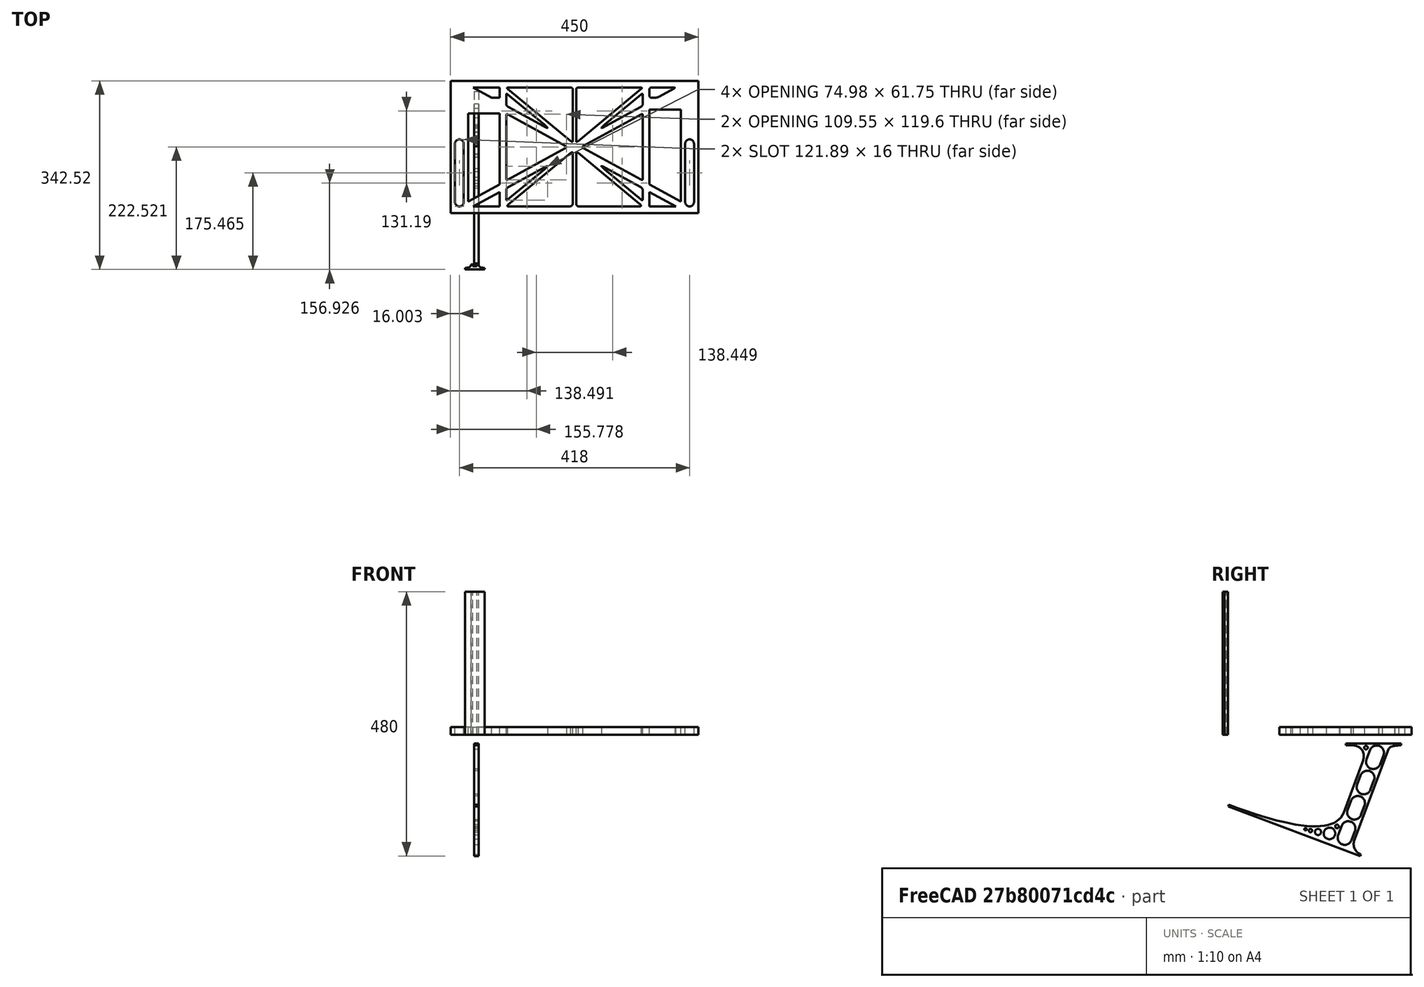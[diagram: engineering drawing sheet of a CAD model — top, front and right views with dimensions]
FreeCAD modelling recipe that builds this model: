
FCSTD DOCUMENT  (FreeCAD 0.19R0.19.2)
Label: laptopStand099
License: All rights reserved
LicenseURL: http://en.wikipedia.org/wiki/All_rights_reserved
objects: Sketcher::SketchObject×3, Part::Extrusion×3
note: 6 computed .brp shape members not serialized (recipe doc carries the construction recipe); baked Part::Feature solids carry a one-line shape summary decoded from their .brp

FEATURE [Sketcher::SketchObject] Sketch
  FullyConstrained = true
  sketch-geometry (268):
    g0: LineSegment StartX=-10.9272 StartY=-82.7794 StartZ=0 EndX=46.0728 EndY=-51.4823 EndZ=0
    g1: LineSegment StartX=366.073 StartY=-91.7794 StartZ=0 EndX=318.073 EndY=-65.424 EndZ=0
    g2: LineSegment StartX=-10.9272 StartY=77.3346 StartZ=0 EndX=-10.9272 EndY=-82.7794 EndZ=0
    g3: LineSegment StartX=375.073 StartY=-82.7794 StartZ=0 EndX=375.073 EndY=83.9235 EndZ=0
    g4: LineSegment StartX=-1.92719 StartY=-91.7794 StartZ=0 EndX=46.0728 EndY=-91.7794 EndZ=0
    g5: LineSegment StartX=318.073 StartY=83.9235 StartZ=0 EndX=318.073 EndY=-51.4823 EndZ=0
    g6: LineSegment StartX=318.073 StartY=-51.4823 StartZ=0 EndX=375.073 EndY=-82.7794 EndZ=0
    g7: LineSegment StartX=318.073 StartY=-65.424 StartZ=0 EndX=318.073 EndY=-91.7794 EndZ=0
    g8: LineSegment StartX=318.073 StartY=-91.7794 StartZ=0 EndX=366.073 EndY=-91.7794 EndZ=0
    g9: LineSegment StartX=46.0728 StartY=-65.424 StartZ=0 EndX=-1.92719 EndY=-91.7794 EndZ=0
    g10: LineSegment StartX=46.0728 StartY=-65.424 StartZ=0 EndX=46.0728 EndY=-91.7794 EndZ=0
    g11: LineSegment StartX=46.0728 StartY=77.3346 StartZ=0 EndX=46.0728 EndY=-51.4823 EndZ=0
    g12: LineSegment StartX=-42.9272 StartY=136.221 StartZ=0 EndX=-42.9272 EndY=-103.779 EndZ=0
    g13: LineSegment StartX=407.073 StartY=136.221 StartZ=0 EndX=407.073 EndY=-103.779 EndZ=0
    g14: ArcOfCircle CenterX=-26.9272 CenterY=22.1087 CenterZ=0 NormalX=0 NormalY=0 NormalZ=1 AngleXU=0 Radius=8 StartAngle=1e-16 EndAngle=3.14159
    g15: ArcOfCircle CenterX=-26.9272 CenterY=-83.7794 CenterZ=0 NormalX=0 NormalY=0 NormalZ=1 AngleXU=0 Radius=8 StartAngle=3.14159 EndAngle=6.28319
    g16: LineSegment StartX=-34.9272 StartY=22.1087 StartZ=0 EndX=-34.9272 EndY=-83.7794 EndZ=0
    g17: LineSegment StartX=-18.9272 StartY=22.1087 StartZ=0 EndX=-18.9272 EndY=-83.7794 EndZ=0
    g18: ArcOfCircle CenterX=391.073 CenterY=22.1087 CenterZ=0 NormalX=0 NormalY=0 NormalZ=1 AngleXU=0 Radius=8 StartAngle=-4.4e-15 EndAngle=3.14159
    g19: LineSegment StartX=399.073 StartY=22.1087 StartZ=0 EndX=399.073 EndY=-83.7794 EndZ=0
    g20: LineSegment StartX=383.073 StartY=22.1087 StartZ=0 EndX=383.073 EndY=-83.7794 EndZ=0
    g21: ArcOfCircle CenterX=391.073 CenterY=-83.7794 CenterZ=0 NormalX=0 NormalY=0 NormalZ=1 AngleXU=0 Radius=8 StartAngle=3.14159 EndAngle=6.28319
    g22: Circle CenterX=175.022 CenterY=27.0628 CenterZ=0 NormalX=0 NormalY=0 NormalZ=1 AngleXU=0 Radius=1
    g23: Circle CenterX=179.022 CenterY=24.8665 CenterZ=0 NormalX=0 NormalY=0 NormalZ=1 AngleXU=0 Radius=1
    g24: Circle CenterX=179.022 CenterY=27.0628 CenterZ=0 NormalX=0 NormalY=0 NormalZ=1 AngleXU=0 Radius=1
    g25: BSplineCurve PolesCount=3 KnotsCount=2 Degree=2 IsPeriodic=0
    g26: GeomPoint X=175.022 Y=27.0628 Z=0
    g27: GeomPoint X=179.022 Y=27.0628 Z=0
    g28: Circle CenterX=189.124 CenterY=27.0628 CenterZ=0 NormalX=0 NormalY=0 NormalZ=1 AngleXU=0 Radius=1
    g29: Circle CenterX=185.124 CenterY=24.8665 CenterZ=0 NormalX=0 NormalY=0 NormalZ=1 AngleXU=0 Radius=1
    g30: Circle CenterX=185.124 CenterY=27.0628 CenterZ=0 NormalX=0 NormalY=0 NormalZ=1 AngleXU=0 Radius=1
    g31: BSplineCurve PolesCount=3 KnotsCount=2 Degree=2 IsPeriodic=0
    g32: GeomPoint X=189.124 Y=27.0628 Z=0
    g33: GeomPoint X=185.124 Y=27.0628 Z=0
    g34: Circle CenterX=175.022 CenterY=5.37834 CenterZ=0 NormalX=0 NormalY=0 NormalZ=1 AngleXU=0 Radius=1
    g35: Circle CenterX=179.022 CenterY=7.57463 CenterZ=0 NormalX=0 NormalY=0 NormalZ=1 AngleXU=0 Radius=1
    g36: Circle CenterX=179.022 CenterY=5.34704 CenterZ=0 NormalX=0 NormalY=0 NormalZ=1 AngleXU=0 Radius=1
    g37: BSplineCurve PolesCount=3 KnotsCount=2 Degree=2 IsPeriodic=0
    g38: GeomPoint X=175.022 Y=5.37834 Z=0
    g39: GeomPoint X=179.022 Y=5.34704 Z=0
    g40: Circle CenterX=189.124 CenterY=5.37834 CenterZ=0 NormalX=0 NormalY=0 NormalZ=1 AngleXU=0 Radius=1
    g41: Circle CenterX=185.124 CenterY=7.57463 CenterZ=0 NormalX=0 NormalY=0 NormalZ=1 AngleXU=0 Radius=1
    g42: Circle CenterX=185.124 CenterY=5.34704 CenterZ=0 NormalX=0 NormalY=0 NormalZ=1 AngleXU=0 Radius=1
    g43: BSplineCurve PolesCount=3 KnotsCount=2 Degree=2 IsPeriodic=0
    g44: GeomPoint X=189.124 Y=5.37834 Z=0
    g45: GeomPoint X=185.124 Y=5.34704 Z=0
    g46: Circle CenterX=165.871 CenterY=18.1458 CenterZ=0 NormalX=0 NormalY=0 NormalZ=1 AngleXU=0 Radius=1
    g47: Circle CenterX=169.377 CenterY=16.2206 CenterZ=0 NormalX=0 NormalY=0 NormalZ=1 AngleXU=0 Radius=1
    g48: Circle CenterX=165.871 CenterY=14.2954 CenterZ=0 NormalX=0 NormalY=0 NormalZ=1 AngleXU=0 Radius=1
    g49: BSplineCurve PolesCount=3 KnotsCount=2 Degree=2 IsPeriodic=0
    g50: GeomPoint X=165.871 Y=18.1458 Z=0
    g51: GeomPoint X=165.871 Y=14.2954 Z=0
    g52: Circle CenterX=198.275 CenterY=18.1458 CenterZ=0 NormalX=0 NormalY=0 NormalZ=1 AngleXU=0 Radius=1
    g53: Circle CenterX=194.768 CenterY=16.2206 CenterZ=0 NormalX=0 NormalY=0 NormalZ=1 AngleXU=0 Radius=1
    g54: Circle CenterX=198.275 CenterY=14.2954 CenterZ=0 NormalX=0 NormalY=0 NormalZ=1 AngleXU=0 Radius=1
    g55: BSplineCurve PolesCount=3 KnotsCount=2 Degree=2 IsPeriodic=0
    g56: GeomPoint X=198.275 Y=18.1458 Z=0
    g57: GeomPoint X=198.275 Y=14.2954 Z=0
    g58: LineSegment StartX=407.073 StartY=-103.779 StartZ=0 EndX=-42.9272 EndY=-103.779 EndZ=0
    g59: LineSegment StartX=407.073 StartY=136.221 StartZ=0 EndX=-42.9272 EndY=136.221 EndZ=0
    g60: LineSegment StartX=46.0728 StartY=77.3346 StartZ=0 EndX=-10.9272 EndY=77.3346 EndZ=0
    g61: LineSegment StartX=46.0728 StartY=105.865 StartZ=0 EndX=31.5028 EndY=105.865 EndZ=0
    g62: LineSegment StartX=46.0728 StartY=124.221 StartZ=0 EndX=46.0728 EndY=105.865 EndZ=0
    g63: LineSegment StartX=-1.92719 StartY=124.221 StartZ=0 EndX=31.5028 EndY=105.865 EndZ=0
    g64: LineSegment StartX=46.0728 StartY=124.221 StartZ=0 EndX=-1.92719 EndY=124.221 EndZ=0
    g65: LineSegment StartX=318.073 StartY=83.9235 StartZ=0 EndX=375.073 EndY=83.9235 EndZ=0
    g66: Circle CenterX=125.607 CenterY=54.1951 CenterZ=0 NormalX=0 NormalY=0 NormalZ=1 AngleXU=0 Radius=1
    g67: Circle CenterX=139.632 CenterY=46.4944 CenterZ=0 NormalX=0 NormalY=0 NormalZ=1 AngleXU=0 Radius=1
    g68: Circle CenterX=127.326 CenterY=56.7187 CenterZ=0 NormalX=0 NormalY=0 NormalZ=1 AngleXU=0 Radius=1
    g69: BSplineCurve PolesCount=3 KnotsCount=2 Degree=2 IsPeriodic=0
    g70: GeomPoint X=125.607 Y=54.1951 Z=0
    g71: GeomPoint X=127.326 Y=56.7187 Z=0
    g72: Circle CenterX=236.821 CenterY=56.7187 CenterZ=0 NormalX=0 NormalY=0 NormalZ=1 AngleXU=0 Radius=1
    g73: Circle CenterX=224.513 CenterY=46.4944 CenterZ=0 NormalX=0 NormalY=0 NormalZ=1 AngleXU=0 Radius=1
    g74: Circle CenterX=238.538 CenterY=54.1951 CenterZ=0 NormalX=0 NormalY=0 NormalZ=1 AngleXU=0 Radius=1
    g75: BSplineCurve PolesCount=3 KnotsCount=2 Degree=2 IsPeriodic=0
    g76: GeomPoint X=236.821 Y=56.7187 Z=0
    g77: GeomPoint X=238.538 Y=54.1951 Z=0
    g78: Circle CenterX=238.538 CenterY=-21.7539 CenterZ=0 NormalX=0 NormalY=0 NormalZ=1 AngleXU=0 Radius=1
    g79: Circle CenterX=224.513 CenterY=-14.0532 CenterZ=0 NormalX=0 NormalY=0 NormalZ=1 AngleXU=0 Radius=1
    g80: Circle CenterX=236.821 CenterY=-24.2775 CenterZ=0 NormalX=0 NormalY=0 NormalZ=1 AngleXU=0 Radius=1
    g81: BSplineCurve PolesCount=3 KnotsCount=2 Degree=2 IsPeriodic=0
    g82: GeomPoint X=238.538 Y=-21.7539 Z=0
    g83: GeomPoint X=236.821 Y=-24.2775 Z=0
    g84: Circle CenterX=125.607 CenterY=-21.7539 CenterZ=0 NormalX=0 NormalY=0 NormalZ=1 AngleXU=0 Radius=1
    g85: Circle CenterX=139.632 CenterY=-14.0532 CenterZ=0 NormalX=0 NormalY=0 NormalZ=1 AngleXU=0 Radius=1
    g86: Circle CenterX=127.325 CenterY=-24.2775 CenterZ=0 NormalX=0 NormalY=0 NormalZ=1 AngleXU=0 Radius=1
    g87: BSplineCurve PolesCount=3 KnotsCount=2 Degree=2 IsPeriodic=0
    g88: GeomPoint X=125.607 Y=-21.7539 Z=0
    g89: GeomPoint X=127.325 Y=-24.2775 Z=0
    g90: Circle CenterX=302.996 CenterY=111.695 CenterZ=0 NormalX=0 NormalY=0 NormalZ=1 AngleXU=0 Radius=1
    g91: Circle CenterX=306.073 CenterY=114.251 CenterZ=0 NormalX=0 NormalY=0 NormalZ=1 AngleXU=0 Radius=1
    g92: Circle CenterX=306.073 CenterY=110.251 CenterZ=0 NormalX=0 NormalY=0 NormalZ=1 AngleXU=0 Radius=1
    g93: BSplineCurve PolesCount=3 KnotsCount=2 Degree=2 IsPeriodic=0
    g94: GeomPoint X=302.996 Y=111.695 Z=0
    g95: GeomPoint X=306.073 Y=110.251 Z=0
    g96: Circle CenterX=306.073 CenterY=95.2763 CenterZ=0 NormalX=0 NormalY=0 NormalZ=1 AngleXU=0 Radius=1
    g97: Circle CenterX=306.073 CenterY=91.2763 CenterZ=0 NormalX=0 NormalY=0 NormalZ=1 AngleXU=0 Radius=1
    g98: Circle CenterX=302.567 CenterY=89.3511 CenterZ=0 NormalX=0 NormalY=0 NormalZ=1 AngleXU=0 Radius=1
    g99: BSplineCurve PolesCount=3 KnotsCount=2 Degree=2 IsPeriodic=0
    g100: GeomPoint X=306.073 Y=95.2763 Z=0
    g101: GeomPoint X=302.567 Y=89.3511 Z=0
    g102: LineSegment StartX=306.073 StartY=110.251 StartZ=0 EndX=306.073 EndY=95.2763 EndZ=0
    g103: LineSegment StartX=302.996 StartY=111.695 StartZ=0 EndX=236.821 EndY=56.7187 EndZ=0
    g104: LineSegment StartX=238.538 StartY=54.1951 StartZ=0 EndX=302.567 EndY=89.3511 EndZ=0
    g105: Circle CenterX=61.1496 CenterY=111.695 CenterZ=0 NormalX=0 NormalY=0 NormalZ=1 AngleXU=0 Radius=1
    g106: Circle CenterX=58.0728 CenterY=114.251 CenterZ=0 NormalX=0 NormalY=0 NormalZ=1 AngleXU=0 Radius=1
    g107: Circle CenterX=58.0728 CenterY=110.251 CenterZ=0 NormalX=0 NormalY=0 NormalZ=1 AngleXU=0 Radius=1
    g108: BSplineCurve PolesCount=3 KnotsCount=2 Degree=2 IsPeriodic=0
    g109: GeomPoint X=61.1496 Y=111.695 Z=0
    g110: GeomPoint X=58.0728 Y=110.251 Z=0
    g111: Circle CenterX=61.5791 CenterY=89.3511 CenterZ=0 NormalX=0 NormalY=0 NormalZ=1 AngleXU=0 Radius=1
    g112: Circle CenterX=58.0728 CenterY=91.2763 CenterZ=0 NormalX=0 NormalY=0 NormalZ=1 AngleXU=0 Radius=1
    g113: Circle CenterX=58.0728 CenterY=95.2763 CenterZ=0 NormalX=0 NormalY=0 NormalZ=1 AngleXU=0 Radius=1
    g114: BSplineCurve PolesCount=3 KnotsCount=2 Degree=2 IsPeriodic=0
    g115: GeomPoint X=61.5791 Y=89.3511 Z=0
    g116: GeomPoint X=58.0728 Y=95.2763 Z=0
    g117: LineSegment StartX=58.0728 StartY=110.251 StartZ=0 EndX=58.0728 EndY=95.2763 EndZ=0
    g118: LineSegment StartX=61.1496 StartY=111.695 StartZ=0 EndX=127.326 EndY=56.7187 EndZ=0
    g119: LineSegment StartX=125.607 StartY=54.1951 StartZ=0 EndX=61.5791 EndY=89.3511 EndZ=0
    g120: Circle CenterX=61.5791 CenterY=-56.9099 CenterZ=0 NormalX=0 NormalY=0 NormalZ=1 AngleXU=0 Radius=1
    g121: Circle CenterX=58.0728 CenterY=-58.8351 CenterZ=0 NormalX=0 NormalY=0 NormalZ=1 AngleXU=0 Radius=1
    g122: Circle CenterX=58.0728 CenterY=-62.8351 CenterZ=0 NormalX=0 NormalY=0 NormalZ=1 AngleXU=0 Radius=1
    g123: BSplineCurve PolesCount=3 KnotsCount=2 Degree=2 IsPeriodic=0
    g124: GeomPoint X=61.5791 Y=-56.9099 Z=0
    g125: GeomPoint X=58.0728 Y=-62.8351 Z=0
    g126: Circle CenterX=58.0728 CenterY=-77.8102 CenterZ=0 NormalX=0 NormalY=0 NormalZ=1 AngleXU=0 Radius=1
    g127: Circle CenterX=58.0728 CenterY=-81.8102 CenterZ=0 NormalX=0 NormalY=0 NormalZ=1 AngleXU=0 Radius=1
    g128: Circle CenterX=61.1496 CenterY=-79.2541 CenterZ=0 NormalX=0 NormalY=0 NormalZ=1 AngleXU=0 Radius=1
    g129: BSplineCurve PolesCount=3 KnotsCount=2 Degree=2 IsPeriodic=0
    g130: GeomPoint X=58.0728 Y=-77.8102 Z=0
    g131: GeomPoint X=61.1496 Y=-79.2541 Z=0
    g132: LineSegment StartX=58.0728 StartY=-62.8351 StartZ=0 EndX=58.0728 EndY=-77.8102 EndZ=0
    g133: LineSegment StartX=61.1496 StartY=-79.2541 StartZ=0 EndX=127.325 EndY=-24.2775 EndZ=0
    g134: LineSegment StartX=125.607 StartY=-21.7539 StartZ=0 EndX=61.5791 EndY=-56.9099 EndZ=0
    g135: Circle CenterX=302.567 CenterY=-56.9099 CenterZ=0 NormalX=0 NormalY=0 NormalZ=1 AngleXU=0 Radius=1
    g136: Circle CenterX=306.073 CenterY=-58.8351 CenterZ=0 NormalX=0 NormalY=0 NormalZ=1 AngleXU=0 Radius=1
    g137: Circle CenterX=306.073 CenterY=-62.8351 CenterZ=0 NormalX=0 NormalY=0 NormalZ=1 AngleXU=0 Radius=1
    g138: BSplineCurve PolesCount=3 KnotsCount=2 Degree=2 IsPeriodic=0
    g139: GeomPoint X=302.567 Y=-56.9099 Z=0
    g140: GeomPoint X=306.073 Y=-62.8351 Z=0
    g141: Circle CenterX=302.996 CenterY=-79.2541 CenterZ=0 NormalX=0 NormalY=0 NormalZ=1 AngleXU=0 Radius=1
    g142: Circle CenterX=306.073 CenterY=-81.8102 CenterZ=0 NormalX=0 NormalY=0 NormalZ=1 AngleXU=0 Radius=1
    g143: Circle CenterX=306.073 CenterY=-77.8102 CenterZ=0 NormalX=0 NormalY=0 NormalZ=1 AngleXU=0 Radius=1
    g144: BSplineCurve PolesCount=3 KnotsCount=2 Degree=2 IsPeriodic=0
    g145: GeomPoint X=302.996 Y=-79.2541 Z=0
    g146: GeomPoint X=306.073 Y=-77.8102 Z=0
    g147: LineSegment StartX=306.073 StartY=-62.8351 StartZ=0 EndX=306.073 EndY=-77.8102 EndZ=0
    g148: LineSegment StartX=302.996 StartY=-79.2541 StartZ=0 EndX=236.821 EndY=-24.2775 EndZ=0
    g149: LineSegment StartX=238.538 StartY=-21.7539 StartZ=0 EndX=302.567 EndY=-56.9099 EndZ=0
    g150: Circle CenterX=61.6457 CenterY=-88.8112 CenterZ=0 NormalX=0 NormalY=0 NormalZ=1 AngleXU=0 Radius=1
    g151: Circle CenterX=58.0728 CenterY=-91.7794 CenterZ=0 NormalX=0 NormalY=0 NormalZ=1 AngleXU=0 Radius=1
    g152: Circle CenterX=63.9135 CenterY=-91.7794 CenterZ=0 NormalX=0 NormalY=0 NormalZ=1 AngleXU=0 Radius=1
    g153: BSplineCurve PolesCount=3 KnotsCount=2 Degree=2 IsPeriodic=0
    g154: GeomPoint X=61.6457 Y=-88.8112 Z=0
    g155: GeomPoint X=63.9135 Y=-91.7794 Z=0
    g156: Circle CenterX=179.022 CenterY=-85.8163 CenterZ=0 NormalX=0 NormalY=0 NormalZ=1 AngleXU=0 Radius=1
    g157: Circle CenterX=179.022 CenterY=-91.7794 CenterZ=0 NormalX=0 NormalY=0 NormalZ=1 AngleXU=0 Radius=1
    g158: Circle CenterX=171.895 CenterY=-91.7794 CenterZ=0 NormalX=0 NormalY=0 NormalZ=1 AngleXU=0 Radius=1
    g159: BSplineCurve PolesCount=3 KnotsCount=2 Degree=2 IsPeriodic=0
    g160: GeomPoint X=179.022 Y=-85.8163 Z=0
    g161: GeomPoint X=171.895 Y=-91.7794 Z=0
    g162: Circle CenterX=185.124 CenterY=-86.2028 CenterZ=0 NormalX=0 NormalY=0 NormalZ=1 AngleXU=0 Radius=1
    g163: Circle CenterX=185.124 CenterY=-91.7794 CenterZ=0 NormalX=0 NormalY=0 NormalZ=1 AngleXU=0 Radius=1
    g164: Circle CenterX=191.747 CenterY=-91.7794 CenterZ=0 NormalX=0 NormalY=0 NormalZ=1 AngleXU=0 Radius=1
    g165: BSplineCurve PolesCount=3 KnotsCount=2 Degree=2 IsPeriodic=0
    g166: GeomPoint X=185.124 Y=-86.2028 Z=0
    g167: GeomPoint X=191.747 Y=-91.7794 Z=0
    g168: Circle CenterX=299.888 CenterY=-86.6413 CenterZ=0 NormalX=0 NormalY=0 NormalZ=1 AngleXU=0 Radius=1
    g169: Circle CenterX=306.073 CenterY=-91.7794 CenterZ=0 NormalX=0 NormalY=0 NormalZ=1 AngleXU=0 Radius=1
    g170: Circle CenterX=298.776 CenterY=-91.7794 CenterZ=0 NormalX=0 NormalY=0 NormalZ=1 AngleXU=0 Radius=1
    g171: BSplineCurve PolesCount=3 KnotsCount=2 Degree=2 IsPeriodic=0
    g172: GeomPoint X=299.888 Y=-86.6413 Z=0
    g173: GeomPoint X=298.776 Y=-91.7794 Z=0
    g174: LineSegment StartX=189.124 StartY=5.37834 StartZ=0 EndX=299.888 EndY=-86.6413 EndZ=0
    g175: LineSegment StartX=298.776 StartY=-91.7794 StartZ=0 EndX=191.747 EndY=-91.7794 EndZ=0
    g176: LineSegment StartX=185.124 StartY=-86.2028 StartZ=0 EndX=185.124 EndY=5.34704 EndZ=0
    g177: LineSegment StartX=179.022 StartY=5.34704 StartZ=0 EndX=179.022 EndY=-85.8163 EndZ=0
    g178: LineSegment StartX=171.895 StartY=-91.7794 StartZ=0 EndX=63.9135 EndY=-91.7794 EndZ=0
    g179: LineSegment StartX=61.6457 StartY=-88.8112 StartZ=0 EndX=175.022 EndY=5.37834 EndZ=0
    g180: Circle CenterX=302.073 CenterY=124.221 CenterZ=0 NormalX=0 NormalY=0 NormalZ=1 AngleXU=0 Radius=1
    g181: Circle CenterX=306.073 CenterY=124.221 CenterZ=0 NormalX=0 NormalY=0 NormalZ=1 AngleXU=0 Radius=1
    g182: Circle CenterX=302.996 CenterY=121.665 CenterZ=0 NormalX=0 NormalY=0 NormalZ=1 AngleXU=0 Radius=1
    g183: BSplineCurve PolesCount=3 KnotsCount=2 Degree=2 IsPeriodic=0
    g184: GeomPoint X=302.073 Y=124.221 Z=0
    g185: GeomPoint X=302.996 Y=121.665 Z=0
    g186: Circle CenterX=189.124 CenterY=124.221 CenterZ=0 NormalX=0 NormalY=0 NormalZ=1 AngleXU=0 Radius=1
    g187: Circle CenterX=185.124 CenterY=124.221 CenterZ=0 NormalX=0 NormalY=0 NormalZ=1 AngleXU=0 Radius=1
    g188: Circle CenterX=185.124 CenterY=120.221 CenterZ=0 NormalX=0 NormalY=0 NormalZ=1 AngleXU=0 Radius=1
    g189: BSplineCurve PolesCount=3 KnotsCount=2 Degree=2 IsPeriodic=0
    g190: GeomPoint X=189.124 Y=124.221 Z=0
    g191: GeomPoint X=185.124 Y=120.221 Z=0
    g192: Circle CenterX=175.022 CenterY=124.221 CenterZ=0 NormalX=0 NormalY=0 NormalZ=1 AngleXU=0 Radius=1
    g193: Circle CenterX=179.022 CenterY=124.221 CenterZ=0 NormalX=0 NormalY=0 NormalZ=1 AngleXU=0 Radius=1
    g194: Circle CenterX=179.022 CenterY=120.221 CenterZ=0 NormalX=0 NormalY=0 NormalZ=1 AngleXU=0 Radius=1
    g195: BSplineCurve PolesCount=3 KnotsCount=2 Degree=2 IsPeriodic=0
    g196: GeomPoint X=175.022 Y=124.221 Z=0
    g197: GeomPoint X=179.022 Y=120.221 Z=0
    g198: Circle CenterX=62.0728 CenterY=124.221 CenterZ=0 NormalX=0 NormalY=0 NormalZ=1 AngleXU=0 Radius=1
    g199: Circle CenterX=58.0728 CenterY=124.221 CenterZ=0 NormalX=0 NormalY=0 NormalZ=1 AngleXU=0 Radius=1
    g200: Circle CenterX=61.1496 CenterY=121.665 CenterZ=0 NormalX=0 NormalY=0 NormalZ=1 AngleXU=0 Radius=1
    g201: BSplineCurve PolesCount=3 KnotsCount=2 Degree=2 IsPeriodic=0
    g202: GeomPoint X=62.0728 Y=124.221 Z=0
    g203: GeomPoint X=61.1496 Y=121.665 Z=0
    g204: LineSegment StartX=62.0728 StartY=124.221 StartZ=0 EndX=175.022 EndY=124.221 EndZ=0
    g205: LineSegment StartX=179.022 StartY=120.221 StartZ=0 EndX=179.022 EndY=27.0628 EndZ=0
    g206: LineSegment StartX=185.124 StartY=27.0628 StartZ=0 EndX=185.124 EndY=120.221 EndZ=0
    g207: LineSegment StartX=189.124 StartY=124.221 StartZ=0 EndX=302.073 EndY=124.221 EndZ=0
    g208: LineSegment StartX=302.996 StartY=121.665 StartZ=0 EndX=189.124 EndY=27.0628 EndZ=0
    g209: LineSegment StartX=175.022 StartY=27.0628 StartZ=0 EndX=61.1496 EndY=121.665 EndZ=0
    g210: Circle CenterX=61.5791 CenterY=75.4095 CenterZ=0 NormalX=0 NormalY=0 NormalZ=1 AngleXU=0 Radius=1
    g211: Circle CenterX=58.0728 CenterY=77.3346 CenterZ=0 NormalX=0 NormalY=0 NormalZ=1 AngleXU=0 Radius=1
    g212: Circle CenterX=58.0728 CenterY=73.3346 CenterZ=0 NormalX=0 NormalY=0 NormalZ=1 AngleXU=0 Radius=1
    g213: BSplineCurve PolesCount=3 KnotsCount=2 Degree=2 IsPeriodic=0
    g214: GeomPoint X=61.5791 Y=75.4095 Z=0
    g215: GeomPoint X=58.0728 Y=73.3346 Z=0
    g216: Circle CenterX=58.0728 CenterY=-40.8935 CenterZ=0 NormalX=0 NormalY=0 NormalZ=1 AngleXU=0 Radius=1
    g217: Circle CenterX=58.0728 CenterY=-44.8935 CenterZ=0 NormalX=0 NormalY=0 NormalZ=1 AngleXU=0 Radius=1
    g218: Circle CenterX=61.5791 CenterY=-42.9683 CenterZ=0 NormalX=0 NormalY=0 NormalZ=1 AngleXU=0 Radius=1
    g219: BSplineCurve PolesCount=3 KnotsCount=2 Degree=2 IsPeriodic=0
    g220: GeomPoint X=58.0728 Y=-40.8935 Z=0
    g221: GeomPoint X=61.5791 Y=-42.9683 Z=0
    g222: LineSegment StartX=61.5791 StartY=-42.9683 StartZ=0 EndX=165.871 EndY=14.2954 EndZ=0
    g223: LineSegment StartX=165.871 StartY=18.1458 StartZ=0 EndX=61.5791 EndY=75.4095 EndZ=0
    g224: LineSegment StartX=58.0728 StartY=73.3346 StartZ=0 EndX=58.0728 EndY=-40.8935 EndZ=0
    g225: Circle CenterX=302.567 CenterY=-42.9683 CenterZ=0 NormalX=0 NormalY=0 NormalZ=1 AngleXU=0 Radius=1
    g226: Circle CenterX=306.073 CenterY=-44.8935 CenterZ=0 NormalX=0 NormalY=0 NormalZ=1 AngleXU=0 Radius=1
    g227: Circle CenterX=306.073 CenterY=-40.8935 CenterZ=0 NormalX=0 NormalY=0 NormalZ=1 AngleXU=0 Radius=1
    g228: BSplineCurve PolesCount=3 KnotsCount=2 Degree=2 IsPeriodic=0
    g229: GeomPoint X=302.567 Y=-42.9683 Z=0
    g230: GeomPoint X=306.073 Y=-40.8935 Z=0
    g231: Circle CenterX=306.073 CenterY=73.3346 CenterZ=0 NormalX=0 NormalY=0 NormalZ=1 AngleXU=0 Radius=1
    g232: Circle CenterX=306.073 CenterY=77.3346 CenterZ=0 NormalX=0 NormalY=0 NormalZ=1 AngleXU=0 Radius=1
    g233: Circle CenterX=302.567 CenterY=75.4095 CenterZ=0 NormalX=0 NormalY=0 NormalZ=1 AngleXU=0 Radius=1
    g234: BSplineCurve PolesCount=3 KnotsCount=2 Degree=2 IsPeriodic=0
    g235: GeomPoint X=306.073 Y=73.3346 Z=0
    g236: GeomPoint X=302.567 Y=75.4095 Z=0
    g237: LineSegment StartX=302.567 StartY=-42.9683 StartZ=0 EndX=198.275 EndY=14.2954 EndZ=0
    g238: LineSegment StartX=198.275 StartY=18.1458 StartZ=0 EndX=302.567 EndY=75.4095 EndZ=0
    g239: LineSegment StartX=306.073 StartY=73.3346 StartZ=0 EndX=306.073 EndY=-40.8935 EndZ=0
    g240: LineSegment StartX=322.073 StartY=105.865 StartZ=0 EndX=328.643 EndY=105.865 EndZ=0
    g241: LineSegment StartX=318.073 StartY=120.221 StartZ=0 EndX=318.073 EndY=109.865 EndZ=0
    g242: LineSegment StartX=336.157 StartY=107.779 StartZ=0 EndX=362.567 EndY=122.294 EndZ=0
    g243: Circle CenterX=362.073 CenterY=124.221 CenterZ=0 NormalX=0 NormalY=0 NormalZ=1 AngleXU=0 Radius=1
    g244: Circle CenterX=366.073 CenterY=124.221 CenterZ=0 NormalX=0 NormalY=0 NormalZ=1 AngleXU=0 Radius=1
    g245: Circle CenterX=362.567 CenterY=122.294 CenterZ=0 NormalX=0 NormalY=0 NormalZ=1 AngleXU=0 Radius=1
    g246: BSplineCurve PolesCount=3 KnotsCount=2 Degree=2 IsPeriodic=0
    g247: GeomPoint X=362.073 Y=124.221 Z=0
    g248: GeomPoint X=362.567 Y=122.294 Z=0
    g249: Circle CenterX=322.073 CenterY=124.221 CenterZ=0 NormalX=0 NormalY=0 NormalZ=1 AngleXU=0 Radius=1
    g250: Circle CenterX=318.073 CenterY=124.221 CenterZ=0 NormalX=0 NormalY=0 NormalZ=1 AngleXU=0 Radius=1
    g251: Circle CenterX=318.073 CenterY=120.221 CenterZ=0 NormalX=0 NormalY=0 NormalZ=1 AngleXU=0 Radius=1
    g252: BSplineCurve PolesCount=3 KnotsCount=2 Degree=2 IsPeriodic=0
    g253: GeomPoint X=322.073 Y=124.221 Z=0
    g254: GeomPoint X=318.073 Y=120.221 Z=0
    g255: Circle CenterX=322.073 CenterY=105.865 CenterZ=0 NormalX=0 NormalY=0 NormalZ=1 AngleXU=0 Radius=1
    g256: Circle CenterX=318.073 CenterY=105.865 CenterZ=0 NormalX=0 NormalY=0 NormalZ=1 AngleXU=0 Radius=1
    g257: Circle CenterX=318.073 CenterY=109.865 CenterZ=0 NormalX=0 NormalY=0 NormalZ=1 AngleXU=0 Radius=1
    g258: BSplineCurve PolesCount=3 KnotsCount=2 Degree=2 IsPeriodic=0
    g259: GeomPoint X=322.073 Y=105.865 Z=0
    g260: GeomPoint X=318.073 Y=109.865 Z=0
    g261: Circle CenterX=336.157 CenterY=107.779 CenterZ=0 NormalX=0 NormalY=0 NormalZ=1 AngleXU=0 Radius=1
    g262: Circle CenterX=332.651 CenterY=105.853 CenterZ=0 NormalX=0 NormalY=0 NormalZ=1 AngleXU=0 Radius=1
    g263: Circle CenterX=328.643 CenterY=105.865 CenterZ=0 NormalX=0 NormalY=0 NormalZ=1 AngleXU=0 Radius=1
    g264: BSplineCurve PolesCount=3 KnotsCount=2 Degree=2 IsPeriodic=0
    g265: GeomPoint X=336.157 Y=107.779 Z=0
    g266: GeomPoint X=328.643 Y=105.865 Z=0
    g267: LineSegment StartX=322.073 StartY=124.221 StartZ=0 EndX=362.073 EndY=124.221 EndZ=0
  constraints (449):
    c: Horizontal(g4)
    c: Coincident(g5,g6)
    c: Coincident(g7,g1)
    c: Tangent(g5,g7)
    c: Coincident(g10,g9)
    c: Coincident(g0,g11)
    c: Block(g6)
    c: Block(g3)
    c: Block(g1)
    c: Block(g7)
    c: Block(g10)
    c: Block(g9)
    c: Block(g0)
    c: Block(g2)
    c: Block(g8)
    c: Block(g4)
    c: Vertical(g12)
    c: Vertical(g13)
    c: Block(g13)
    c: Block(g12)
    c: Tangent(g14,g17) = 1.5708
    c: Tangent(g14,g16) = -1.5708
    c: Tangent(g16,g15) = -1.5708
    c: Tangent(g17,g15) = 1.5708
    c: Vertical(g16)
    c: Equal(g14,g15)
    c: Block(g17)
    c: Block(g16)
    c: Tangent(g18,g19) = 1.5708
    c: Tangent(g19,g21) = 1.5708
    c: Equal(g18,g21)
    c: Coincident(g20,g18)
    c: Coincident(g20,g21)
    c: Block(g19)
    c: Block(g20)
    c: Weight(g22) = 1
    c: Equal(g22,g23)
    c: Equal(g22,g24)
    c: InternalAlignment(g22,g25)
    c: InternalAlignment(g23,g25)
    c: InternalAlignment(g24,g25)
    c: InternalAlignment(g26,g25)
    c: InternalAlignment(g27,g25)
    c: Weight(g28) = 1
    c: Equal(g28,g29)
    c: Equal(g28,g30)
    c: InternalAlignment(g28,g31)
    c: InternalAlignment(g29,g31)
    c: InternalAlignment(g30,g31)
    c: InternalAlignment(g32,g31)
    c: InternalAlignment(g33,g31)
    c: Block(g31)
    c: Block(g25)
    c: Weight(g34) = 1
    c: Equal(g34,g35)
    c: Equal(g34,g36)
    c: InternalAlignment(g34,g37)
    c: InternalAlignment(g35,g37)
    c: InternalAlignment(g36,g37)
    c: InternalAlignment(g38,g37)
    c: InternalAlignment(g39,g37)
    c: Weight(g40) = 1
    c: Equal(g40,g41)
    c: Equal(g40,g42)
    c: InternalAlignment(g40,g43)
    c: InternalAlignment(g41,g43)
    c: InternalAlignment(g42,g43)
    c: InternalAlignment(g44,g43)
    c: InternalAlignment(g45,g43)
    c: Block(g43)
    c: Block(g37)
    c: Weight(g46) = 1
    c: Equal(g46,g47)
    c: Equal(g46,g48)
    c: InternalAlignment(g46,g49)
    c: InternalAlignment(g47,g49)
    c: InternalAlignment(g48,g49)
    c: InternalAlignment(g50,g49)
    c: InternalAlignment(g51,g49)
    c: Weight(g52) = 1
    c: Equal(g52,g53)
    c: Equal(g52,g54)
    c: InternalAlignment(g52,g55)
    c: InternalAlignment(g53,g55)
    c: InternalAlignment(g54,g55)
    c: InternalAlignment(g56,g55)
    c: InternalAlignment(g57,g55)
    c: Block(g49)
    c: Block(g55)
    c: Coincident(g58,g13)
    c: Coincident(g58,g12)
    c: Horizontal(g58)
    c: Distance(g58) = 450
    c: Coincident(g59,g13)
    c: Coincident(g59,g12)
    c: Horizontal(g59)
    c: Horizontal(g60)
    c: Coincident(g11,g60)
    c: Horizontal(g61)
    c: Vertical(g62)
    c: Block(g62)
    c: Block(g61)
    c: Block(g60)
    c: Distance(g62) = 18.3554
    c: Coincident(g64,g62)
    c: Coincident(g64,g63)
    c: Horizontal(g64)
    c: Block(g64)
    c: Block(g63)
    c: Coincident(g61,g63)
    c: Coincident(g2,g60)
    c: Coincident(g65,g5)
    c: Horizontal(g65)
    c: Block(g65)
    c: Coincident(g3,g65)
    c: Weight(g66) = 1
    c: Equal(g66,g67)
    c: Equal(g66,g68)
    c: InternalAlignment(g66,g69)
    c: InternalAlignment(g67,g69)
    c: InternalAlignment(g68,g69)
    c: InternalAlignment(g70,g69)
    c: InternalAlignment(g71,g69)
    c: Block(g69)
    c: Weight(g72) = 1
    c: Equal(g72,g73)
    c: Equal(g72,g74)
    c: InternalAlignment(g72,g75)
    c: InternalAlignment(g73,g75)
    c: InternalAlignment(g74,g75)
    c: InternalAlignment(g76,g75)
    c: InternalAlignment(g77,g75)
    c: Block(g75)
    c: Weight(g78) = 1
    c: Equal(g78,g79)
    c: Equal(g78,g80)
    c: InternalAlignment(g78,g81)
    c: InternalAlignment(g79,g81)
    c: InternalAlignment(g80,g81)
    c: InternalAlignment(g82,g81)
    c: InternalAlignment(g83,g81)
    c: Block(g81)
    c: Weight(g84) = 1
    c: Equal(g84,g85)
    c: Equal(g84,g86)
    c: InternalAlignment(g84,g87)
    c: InternalAlignment(g85,g87)
    c: InternalAlignment(g86,g87)
    c: InternalAlignment(g88,g87)
    c: InternalAlignment(g89,g87)
    c: Block(g87)
    c: Weight(g90) = 1
    c: Equal(g90,g91)
    c: Equal(g90,g92)
    c: InternalAlignment(g90,g93)
    c: InternalAlignment(g91,g93)
    c: InternalAlignment(g92,g93)
    c: InternalAlignment(g94,g93)
    c: InternalAlignment(g95,g93)
    c: Weight(g96) = 1
    c: Equal(g96,g97)
    c: Equal(g96,g98)
    c: InternalAlignment(g96,g99)
    c: InternalAlignment(g97,g99)
    c: InternalAlignment(g98,g99)
    c: InternalAlignment(g100,g99)
    c: InternalAlignment(g101,g99)
    c: Block(g93)
    c: Block(g99)
    c: Coincident(g102,g93)
    c: Coincident(g102,g99)
    c: Vertical(g102)
    c: Coincident(g103,g93)
    c: Coincident(g103,g75)
    c: Coincident(g104,g75)
    c: Coincident(g104,g99)
    c: Weight(g105) = 1
    c: Equal(g105,g106)
    c: Equal(g105,g107)
    c: InternalAlignment(g105,g108)
    c: InternalAlignment(g106,g108)
    c: InternalAlignment(g107,g108)
    c: InternalAlignment(g109,g108)
    c: InternalAlignment(g110,g108)
    c: Weight(g111) = 1
    c: Equal(g111,g112)
    c: Equal(g111,g113)
    c: InternalAlignment(g111,g114)
    c: InternalAlignment(g112,g114)
    c: InternalAlignment(g113,g114)
    c: InternalAlignment(g115,g114)
    c: InternalAlignment(g116,g114)
    c: Block(g108)
    c: Block(g114)
    c: Coincident(g117,g108)
    c: Coincident(g117,g114)
    c: Vertical(g117)
    c: Coincident(g118,g108)
    c: Coincident(g118,g69)
    c: Coincident(g119,g69)
    c: Coincident(g119,g114)
    c: Weight(g120) = 1
    c: Equal(g120,g121)
    c: Equal(g120,g122)
    c: InternalAlignment(g120,g123)
    c: InternalAlignment(g121,g123)
    c: InternalAlignment(g122,g123)
    c: InternalAlignment(g124,g123)
    c: InternalAlignment(g125,g123)
    c: Weight(g126) = 1
    c: Equal(g126,g127)
    c: Equal(g126,g128)
    c: InternalAlignment(g126,g129)
    c: InternalAlignment(g127,g129)
    c: InternalAlignment(g128,g129)
    c: InternalAlignment(g130,g129)
    c: InternalAlignment(g131,g129)
    c: Block(g123)
    c: Block(g129)
    c: Coincident(g132,g123)
    c: Coincident(g132,g129)
    c: Vertical(g132)
    c: Coincident(g133,g129)
    c: Coincident(g133,g87)
    c: Coincident(g134,g87)
    c: Coincident(g134,g123)
    c: Weight(g135) = 1
    c: Equal(g135,g136)
    c: Equal(g135,g137)
    c: InternalAlignment(g135,g138)
    c: InternalAlignment(g136,g138)
    c: InternalAlignment(g137,g138)
    c: InternalAlignment(g139,g138)
    c: InternalAlignment(g140,g138)
    c: Weight(g141) = 1
    c: Equal(g141,g142)
    c: Equal(g141,g143)
    c: InternalAlignment(g141,g144)
    c: InternalAlignment(g142,g144)
    c: InternalAlignment(g143,g144)
    c: InternalAlignment(g145,g144)
    c: InternalAlignment(g146,g144)
    c: Block(g138)
    c: Block(g144)
    c: Coincident(g147,g138)
    c: Coincident(g147,g144)
    c: Vertical(g147)
    c: Coincident(g148,g144)
    c: Coincident(g148,g81)
    c: Coincident(g149,g81)
    c: Coincident(g149,g138)
    c: Weight(g150) = 1
    c: Equal(g150,g151)
    c: Equal(g150,g152)
    c: InternalAlignment(g150,g153)
    c: InternalAlignment(g151,g153)
    c: InternalAlignment(g152,g153)
    c: InternalAlignment(g154,g153)
    c: InternalAlignment(g155,g153)
    c: Weight(g156) = 1
    c: Equal(g156,g157)
    c: Equal(g156,g158)
    c: InternalAlignment(g156,g159)
    c: InternalAlignment(g157,g159)
    c: InternalAlignment(g158,g159)
    c: InternalAlignment(g160,g159)
    c: InternalAlignment(g161,g159)
    c: Weight(g162) = 1
    c: Equal(g162,g163)
    c: Equal(g162,g164)
    c: InternalAlignment(g162,g165)
    c: InternalAlignment(g163,g165)
    c: InternalAlignment(g164,g165)
    c: InternalAlignment(g166,g165)
    c: InternalAlignment(g167,g165)
    c: Weight(g168) = 1
    c: Equal(g168,g169)
    c: Equal(g168,g170)
    c: InternalAlignment(g168,g171)
    c: InternalAlignment(g169,g171)
    c: InternalAlignment(g170,g171)
    c: InternalAlignment(g172,g171)
    c: InternalAlignment(g173,g171)
    c: Block(g171)
    c: Block(g165)
    c: Block(g159)
    c: Block(g153)
    c: Coincident(g174,g43)
    c: Coincident(g174,g171)
    c: Coincident(g175,g171)
    c: Coincident(g175,g165)
    c: Horizontal(g175)
    c: Coincident(g176,g165)
    c: Coincident(g176,g43)
    c: Vertical(g176)
    c: Coincident(g177,g37)
    c: Coincident(g177,g159)
    c: Vertical(g177)
    c: Coincident(g178,g159)
    c: Coincident(g178,g153)
    c: Horizontal(g178)
    c: Coincident(g179,g153)
    c: Coincident(g179,g37)
    c: Weight(g180) = 1
    c: Equal(g180,g181)
    c: Equal(g180,g182)
    c: InternalAlignment(g180,g183)
    c: InternalAlignment(g181,g183)
    c: InternalAlignment(g182,g183)
    c: InternalAlignment(g184,g183)
    c: InternalAlignment(g185,g183)
    c: Weight(g186) = 1
    c: Equal(g186,g187)
    c: Equal(g186,g188)
    c: InternalAlignment(g186,g189)
    c: InternalAlignment(g187,g189)
    c: InternalAlignment(g188,g189)
    c: InternalAlignment(g190,g189)
    c: InternalAlignment(g191,g189)
    c: Weight(g192) = 1
    c: Equal(g192,g193)
    c: Equal(g192,g194)
    c: InternalAlignment(g192,g195)
    c: InternalAlignment(g193,g195)
    c: InternalAlignment(g194,g195)
    c: InternalAlignment(g196,g195)
    c: InternalAlignment(g197,g195)
    c: Weight(g198) = 1
    c: Equal(g198,g199)
    c: Equal(g198,g200)
    c: InternalAlignment(g198,g201)
    c: InternalAlignment(g199,g201)
    c: InternalAlignment(g200,g201)
    c: InternalAlignment(g202,g201)
    c: InternalAlignment(g203,g201)
    c: Block(g201)
    c: Block(g195)
    c: Block(g189)
    c: Block(g183)
    c: Coincident(g204,g201)
    c: Coincident(g204,g195)
    c: Horizontal(g204)
    c: Coincident(g205,g195)
    c: Coincident(g205,g25)
    c: Vertical(g205)
    c: Coincident(g206,g31)
    c: Coincident(g206,g189)
    c: Vertical(g206)
    c: Coincident(g207,g189)
    c: Coincident(g207,g183)
    c: Horizontal(g207)
    c: Coincident(g208,g183)
    c: Coincident(g208,g31)
    c: Coincident(g209,g25)
    c: Weight(g210) = 1
    c: Equal(g210,g211)
    c: Equal(g210,g212)
    c: InternalAlignment(g210,g213)
    c: InternalAlignment(g211,g213)
    c: InternalAlignment(g212,g213)
    c: InternalAlignment(g214,g213)
    c: InternalAlignment(g215,g213)
    c: Weight(g216) = 1
    c: Equal(g216,g217)
    c: Equal(g216,g218)
    c: InternalAlignment(g216,g219)
    c: InternalAlignment(g217,g219)
    c: InternalAlignment(g218,g219)
    c: InternalAlignment(g220,g219)
    c: InternalAlignment(g221,g219)
    c: Block(g219)
    c: Block(g213)
    c: Coincident(g222,g219)
    c: Coincident(g222,g49)
    c: Coincident(g223,g49)
    c: Coincident(g223,g213)
    c: Coincident(g224,g213)
    c: Coincident(g224,g219)
    c: Vertical(g224)
    c: Weight(g225) = 1
    c: Equal(g225,g226)
    c: Equal(g225,g227)
    c: InternalAlignment(g225,g228)
    c: InternalAlignment(g226,g228)
    c: InternalAlignment(g227,g228)
    c: InternalAlignment(g229,g228)
    c: InternalAlignment(g230,g228)
    c: Weight(g231) = 1
    c: Equal(g231,g232)
    c: Equal(g231,g233)
    c: InternalAlignment(g231,g234)
    c: InternalAlignment(g232,g234)
    c: InternalAlignment(g233,g234)
    c: InternalAlignment(g235,g234)
    c: InternalAlignment(g236,g234)
    c: Block(g234)
    c: Block(g228)
    c: Coincident(g237,g228)
    c: Coincident(g237,g55)
    c: Coincident(g238,g55)
    c: Coincident(g238,g234)
    c: Coincident(g239,g234)
    c: Coincident(g239,g228)
    c: Vertical(g239)
    c: Horizontal(g240)
    c: Block(g240)
    c: Vertical(g241)
    c: Block(g241)
    c: Block(g242)
    c: Weight(g243) = 1
    c: Equal(g243,g244)
    c: Equal(g243,g245)
    c: InternalAlignment(g243,g246)
    c: InternalAlignment(g244,g246)
    c: InternalAlignment(g245,g246)
    c: InternalAlignment(g247,g246)
    c: InternalAlignment(g248,g246)
    c: Weight(g249) = 1
    c: Equal(g249,g250)
    c: Equal(g249,g251)
    c: InternalAlignment(g249,g252)
    c: InternalAlignment(g250,g252)
    c: InternalAlignment(g251,g252)
    c: InternalAlignment(g253,g252)
    c: InternalAlignment(g254,g252)
    c: Weight(g255) = 1
    c: Equal(g255,g256)
    c: Equal(g255,g257)
    c: InternalAlignment(g255,g258)
    c: InternalAlignment(g256,g258)
    c: InternalAlignment(g257,g258)
    c: InternalAlignment(g259,g258)
    c: InternalAlignment(g260,g258)
    c: Weight(g261) = 1
    c: Equal(g261,g262)
    c: Equal(g261,g263)
    c: InternalAlignment(g261,g264)
    c: InternalAlignment(g262,g264)
    c: InternalAlignment(g263,g264)
    c: InternalAlignment(g265,g264)
    c: InternalAlignment(g266,g264)
    c: Block(g246)
    c: Block(g252)
    c: Block(g258)
    c: Block(g264)
    c: Coincident(g267,g252)
    c: Coincident(g267,g246)
    c: Horizontal(g267)
    c: Block(g209)
FEATURE [Sketcher::SketchObject] Sketch001
  FullyConstrained = true
  MapMode = 4
  Placement = pos=(0,0,0) rot=(0.57735,0.57735,0.57735;2.0944rad)
  Support = -> [Sketch]
  sketch-geometry (46):
    g0: BSplineCurve PolesCount=3 KnotsCount=2 Degree=2 IsPeriodic=0
    g1: ArcOfCircle CenterX=73.1223 CenterY=-32.291 CenterZ=0 NormalX=0 NormalY=0 NormalZ=1 AngleXU=0 Radius=13 StartAngle=5.92268 EndAngle=9.06428
    g2: ArcOfCircle CenterX=66.7816 CenterY=-49.1439 CenterZ=0 NormalX=0 NormalY=0 NormalZ=1 AngleXU=0 Radius=13 StartAngle=2.78068 EndAngle=5.92131
    g3: ArcOfCircle CenterX=55.9263 CenterY=-78.1807 CenterZ=0 NormalX=0 NormalY=0 NormalZ=1 AngleXU=0 Radius=13 StartAngle=5.92268 EndAngle=9.06428
    g4: ArcOfCircle CenterX=49.5884 CenterY=-95.0342 CenterZ=0 NormalX=0 NormalY=0 NormalZ=1 AngleXU=0 Radius=13 StartAngle=2.78068 EndAngle=5.92131
    g5: ArcOfCircle CenterX=38.7206 CenterY=-124.067 CenterZ=0 NormalX=0 NormalY=0 NormalZ=1 AngleXU=0 Radius=13 StartAngle=5.92268 EndAngle=9.06428
    g6: ArcOfCircle CenterX=32.3875 CenterY=-140.92 CenterZ=0 NormalX=0 NormalY=0 NormalZ=1 AngleXU=0 Radius=13 StartAngle=2.78068 EndAngle=5.92131
    g7: ArcOfCircle CenterX=21.4715 CenterY=-169.934 CenterZ=0 NormalX=0 NormalY=0 NormalZ=1 AngleXU=0 Radius=13 StartAngle=5.92268 EndAngle=9.06428
    g8: ArcOfCircle CenterX=15.1336 CenterY=-186.787 CenterZ=0 NormalX=0 NormalY=0 NormalZ=1 AngleXU=0 Radius=13 StartAngle=2.78068 EndAngle=5.92131
    g9-g12: Circle x4 (B-spline internal-alignment scaffolding for g13; pole/knot coordinates omitted)
    g13: BSplineCurve PolesCount=4 KnotsCount=2 Degree=3 IsPeriodic=0
    g14: GeomPoint X=28.8094 Y=-19.0875 Z=0
    g15: GeomPoint X=47.0443 Y=-50.4712 Z=0
    g16: Circle CenterX=53.5586 CenterY=-23.2695 CenterZ=0 NormalX=0 NormalY=0 NormalZ=1 AngleXU=0 Radius=3.24518
    g17: Circle CenterX=-195.441 CenterY=-127.082 CenterZ=0 NormalX=0 NormalY=0 NormalZ=1 AngleXU=0 Radius=1
    g18: Circle CenterX=-8.24091 CenterY=-197.481 CenterZ=0 NormalX=0 NormalY=0 NormalZ=1 AngleXU=0 Radius=1
    g19: Circle CenterX=12.8789 CenterY=-141.321 CenterZ=0 NormalX=0 NormalY=0 NormalZ=1 AngleXU=0 Radius=1
    g20: BSplineCurve PolesCount=3 KnotsCount=2 Degree=2 IsPeriodic=0
    g21: GeomPoint X=-195.441 Y=-127.082 Z=0
    g22: GeomPoint X=12.8789 Y=-141.321 Z=0
    g23: Circle CenterX=-12.8016 CenterY=-179.036 CenterZ=0 NormalX=0 NormalY=0 NormalZ=1 AngleXU=0 Radius=10.5072
    g24: Circle CenterX=0.933922 CenterY=-166.43 CenterZ=0 NormalX=0 NormalY=0 NormalZ=1 AngleXU=0 Radius=3.26661
    g25: Circle CenterX=-33.5518 CenterY=-176.44 CenterZ=0 NormalX=0 NormalY=0 NormalZ=1 AngleXU=0 Radius=5.64388
    g26: Circle CenterX=-47.2366 CenterY=-173.859 CenterZ=0 NormalX=0 NormalY=0 NormalZ=1 AngleXU=0 Radius=3.01653
    g27: Circle CenterX=-56.2595 CenterY=-171.456 CenterZ=0 NormalX=0 NormalY=0 NormalZ=1 AngleXU=0 Radius=2.12826
    g28: ArcOfCircle CenterX=51.2151 CenterY=-198.473 CenterZ=0 NormalX=0 NormalY=0 NormalZ=1 AngleXU=0 Radius=20 StartAngle=2.78189 EndAngle=4.35269
    g29: LineSegment StartX=32.4951 StartY=-191.433 StartZ=0 EndX=94.6578 EndY=-26.1352 EndZ=0
    g30: LineSegment StartX=43.1192 StartY=-220.001 StartZ=0 EndX=-196.497 EndY=-129.89 EndZ=0
    g31: LineSegment StartX=43.1192 StartY=-220.001 StartZ=0 EndX=44.1752 EndY=-217.193 EndZ=0
    g32: LineSegment StartX=117.223 StartY=-19.0875 StartZ=0 EndX=117.223 EndY=-16.0875 EndZ=0
    g33: LineSegment StartX=117.223 StartY=-16.0875 StartZ=0 EndX=17.2232 EndY=-16.0875 EndZ=0
    g34: LineSegment StartX=17.2232 StartY=-16.0875 StartZ=0 EndX=17.2232 EndY=-19.0875 EndZ=0
    g35: LineSegment StartX=28.8094 StartY=-19.0875 StartZ=0 EndX=17.2232 EndY=-19.0875 EndZ=0
    g36: LineSegment StartX=47.0443 StartY=-50.4712 StartZ=0 EndX=12.8789 EndY=-141.321 EndZ=0
    g37: LineSegment StartX=-195.441 StartY=-127.082 StartZ=0 EndX=-196.497 EndY=-129.89 EndZ=0
    g38: LineSegment StartX=85.2866 StartY=-36.8766 StartZ=0 EndX=78.9396 EndY=-53.7463 EndZ=0
    g39: LineSegment StartX=60.9579 StartY=-27.7053 StartZ=0 EndX=54.6191 EndY=-44.5532 EndZ=0
    g40: LineSegment StartX=68.0907 StartY=-82.7664 StartZ=0 EndX=61.7465 EndY=-99.6365 EndZ=0
    g41: LineSegment StartX=43.7619 StartY=-73.595 StartZ=0 EndX=37.426 EndY=-90.4435 EndZ=0
    g42: LineSegment StartX=50.885 StartY=-128.652 StartZ=0 EndX=44.5456 EndY=-145.522 EndZ=0
    g43: LineSegment StartX=26.5562 StartY=-119.481 StartZ=0 EndX=20.2251 EndY=-136.329 EndZ=0
    g44: LineSegment StartX=9.3071 StartY=-165.349 StartZ=0 EndX=2.97115 EndY=-182.197 EndZ=0
    g45: LineSegment StartX=33.6358 StartY=-174.52 StartZ=0 EndX=27.2917 EndY=-191.39 EndZ=0
  constraints (71):
    c: Block(g0)
    c: Block(g1)
    c: Block(g2)
    c: Block(g4)
    c: Block(g3)
    c: Block(g6)
    c: Block(g5)
    c: Block(g8)
    c: Block(g7)
    c: Weight(g9) = 1
    c: Equal(g9,g10)
    c: Equal(g9,g11)
    c: Equal(g9,g12)
    c: InternalAlignment(g9-g12 -> g13) x4
    c: InternalAlignment(g14,g13)
    c: InternalAlignment(g15,g13)
    c: Block(g16)
    c: Weight(g17) = 1
    c: Equal(g17,g18)
    c: Equal(g17,g19)
    c: InternalAlignment(g17,g20)
    c: InternalAlignment(g18,g20)
    c: InternalAlignment(g19,g20)
    c: InternalAlignment(g21,g20)
    c: InternalAlignment(g22,g20)
    c: Block(g20)
    c: Block(g23)
    c: Block(g24)
    c: Block(g25)
    c: Block(g26)
    c: Block(g27)
    c: Block(g28)
    c: Coincident(g29,g28)
    c: Coincident(g29,g0)
    c: Block(g13)
    c: Coincident(g31,g30)
    c: Coincident(g31,g28)
    c: Block(g31)
    c: Coincident(g32,g0)
    c: Vertical(g32)
    c: Coincident(g33,g32)
    c: Horizontal(g33)
    c: Coincident(g34,g33)
    c: Vertical(g34)
    c: Block(g33)
    c: Coincident(g35,g13)
    c: Coincident(g35,g34)
    c: Horizontal(g35)
    c: Coincident(g36,g13)
    c: Coincident(g36,g20)
    c: Coincident(g37,g20)
    c: Coincident(g37,g30)
    c: Block(g30)
    c: Coincident(g38,g1)
    c: Coincident(g38,g2)
    c: Coincident(g39,g1)
    c: Coincident(g39,g2)
    c: Coincident(g40,g3)
    c: Coincident(g40,g4)
    c: Coincident(g41,g3)
    c: Coincident(g41,g4)
    c: Coincident(g42,g5)
    c: Coincident(g42,g6)
    c: Coincident(g43,g5)
    c: Coincident(g43,g6)
    c: Coincident(g44,g7)
    c: Coincident(g44,g8)
    c: Coincident(g45,g7)
    c: Coincident(g45,g8)
    c: Distance(g30) = 256
    c: Distance(g33) = 100
FEATURE [Part::Extrusion] Extrude002
  Base = -> Sketch001
  Dir = (1,0,0)
  DirMode = 2
  FaceMakerClass = Part::FaceMakerBullseye
  LengthFwd = 8
  LengthRev = 0
  Solid = true
  Symmetric = false
FEATURE [Sketcher::SketchObject] Sketch002
  FullyConstrained = true
  sketch-geometry (20):
    g0: LineSegment StartX=-2.77179 StartY=-200.304 StartZ=0 EndX=5.22821 EndY=-200.304 EndZ=0
    g1: LineSegment StartX=5.22821 StartY=-200.304 StartZ=0 EndX=5.22821 EndY=-197.304 EndZ=0
    g2: LineSegment StartX=-2.77179 StartY=-200.304 StartZ=0 EndX=-2.77179 EndY=-197.304 EndZ=0
    g3: LineSegment StartX=5.22821 StartY=-197.304 StartZ=0 EndX=8.22821 EndY=-197.304 EndZ=0
    g4: LineSegment StartX=-2.77179 StartY=-197.304 StartZ=0 EndX=-5.77179 EndY=-197.304 EndZ=0
    g5: LineSegment StartX=19.2282 StartY=-203.304 StartZ=0 EndX=19.2282 EndY=-206.304 EndZ=0
    g6: LineSegment StartX=-16.7718 StartY=-203.304 StartZ=0 EndX=-16.7718 EndY=-206.304 EndZ=0
    g7: LineSegment StartX=-16.7718 StartY=-206.304 StartZ=0 EndX=19.2282 EndY=-206.304 EndZ=0
    g8: Circle CenterX=-16.7718 CenterY=-203.304 CenterZ=0 NormalX=0 NormalY=0 NormalZ=1 AngleXU=0 Radius=1
    g9: Circle CenterX=-5.77179 CenterY=-203.304 CenterZ=0 NormalX=0 NormalY=0 NormalZ=1 AngleXU=0 Radius=1
    g10: Circle CenterX=-5.77179 CenterY=-197.304 CenterZ=0 NormalX=0 NormalY=0 NormalZ=1 AngleXU=0 Radius=1
    g11: BSplineCurve PolesCount=3 KnotsCount=2 Degree=2 IsPeriodic=0
    g12: GeomPoint X=-16.7718 Y=-203.304 Z=0
    g13: GeomPoint X=-5.77179 Y=-197.304 Z=0
    g14: Circle CenterX=19.2282 CenterY=-203.304 CenterZ=0 NormalX=0 NormalY=0 NormalZ=1 AngleXU=0 Radius=1
    g15: Circle CenterX=8.22821 CenterY=-203.304 CenterZ=0 NormalX=0 NormalY=0 NormalZ=1 AngleXU=0 Radius=1
    g16: Circle CenterX=8.22821 CenterY=-197.304 CenterZ=0 NormalX=0 NormalY=0 NormalZ=1 AngleXU=0 Radius=1
    g17: BSplineCurve PolesCount=3 KnotsCount=2 Degree=2 IsPeriodic=0
    g18: GeomPoint X=19.2282 Y=-203.304 Z=0
    g19: GeomPoint X=8.22821 Y=-197.304 Z=0
  constraints (41):
    c: Horizontal(g0)
    c: Distance(g0) = 8
    c: Coincident(g1,g0)
    c: Vertical(g1)
    c: Distance(g1) = 3
    c: Coincident(g2,g0)
    c: Vertical(g2)
    c: Distance(g2) = 3
    c: Coincident(g3,g1)
    c: Horizontal(g3)
    c: Distance(g3) = 3
    c: Coincident(g4,g2)
    c: Horizontal(g4)
    c: Distance(g4) = 3
    c: Vertical(g5)
    c: Vertical(g6)
    c: Coincident(g7,g6)
    c: Coincident(g7,g5)
    c: Weight(g8) = 1
    c: Equal(g8,g9)
    c: Equal(g8,g10)
    c: Coincident(g11,g4)
    c: InternalAlignment(g8,g11)
    c: InternalAlignment(g9,g11)
    c: InternalAlignment(g10,g11)
    c: InternalAlignment(g12,g11)
    c: InternalAlignment(g13,g11)
    c: Coincident(g17,g5)
    c: Weight(g14) = 1
    c: Equal(g14,g15)
    c: Equal(g14,g16)
    c: Coincident(g17,g3)
    c: InternalAlignment(g14,g17)
    c: InternalAlignment(g15,g17)
    c: InternalAlignment(g16,g17)
    c: InternalAlignment(g18,g17)
    c: InternalAlignment(g19,g17)
    c: Block(g7)
    c: Block(g17)
    c: Block(g11)
    c: Block(g6)
FEATURE [Part::Extrusion] Extrude003
  Base = -> Sketch002
  Dir = (0,0,1)
  DirMode = 2
  FaceMakerClass = Part::FaceMakerBullseye
  LengthFwd = 260
  LengthRev = 0
  Solid = true
  Symmetric = false
FEATURE [Part::Extrusion] Extrude
  Base = -> Sketch
  Dir = (0,0,1)
  DirMode = 2
  FaceMakerClass = Part::FaceMakerBullseye
  LengthFwd = 14
  LengthRev = 0
  Solid = true
  Symmetric = false
